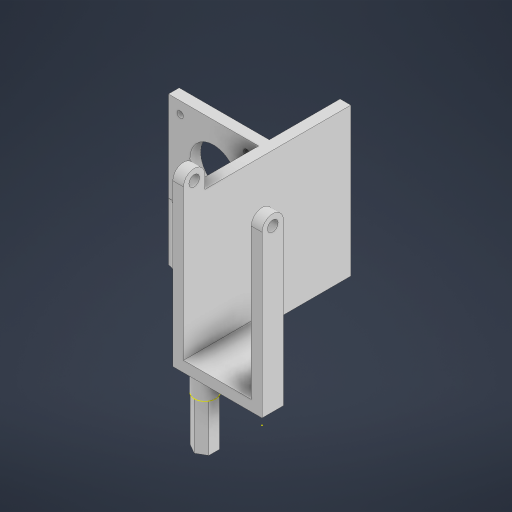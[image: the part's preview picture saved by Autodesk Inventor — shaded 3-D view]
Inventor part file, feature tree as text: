
AUTODESK INVENTOR PART (.ipt)
format: ipt  version: 2024.2 (Build 282272000, 272)  size: 648,192 bytes
history: native  units: mm
features: extrude x13, sketch x12, projected_geometry x4, other x3, chamfer x2, fillet x1
ambient origin geometry x8: Origin, YZ Plane, XZ Plane, XY Plane, X Axis, Y Axis, Z Axis, Center Point
bodies: Body1 (feature_tree)
feature tree (35):
  other  "솔리드1"
  extrude  "돌출1"  Depth=5.0mm
  extrude  "돌출2"  Depth=10.0mm
  extrude  "돌출3"  Depth=53.0mm
  extrude  "돌출4"  Depth=10.0mm
  extrude  "돌출5"  Depth=5.0mm TaperAngle=0.0deg
  chamfer  "모따기1"  Distance=10.0mm
  extrude  "돌출6"  Depth=5.0mm
  extrude  "돌출7"  Depth=31.6mm TaperAngle=0.0deg
  extrude  "돌출8"  Depth=10.0mm
  other  "직접 편집1"
  fillet  "모깎기1"  Radius=53.0mm
  extrude  "돌출9"  Depth=5.0mm
  chamfer  "모따기2"  Distance=5.0mm
  sketch  "스케치11"
  extrude  "돌출10"  Depth=30.0mm TaperAngle=0.0deg
  extrude  "돌출11"  Depth=42.0mm
  extrude  "돌출12"  Depth=42.0mm
  extrude  "돌출13"  Depth=3.0mm
  sketch  "스케치1"
  sketch  "스케치2"
  sketch  "스케치3"
  sketch  "스케치4"
  sketch  "스케치5"
  sketch  "스케치6"
  sketch  "스케치7"
  sketch  "스케치8"
  sketch  "스케치9"
  projected_geometry  "투영된 루프1"
  projected_geometry  "투영된 루프2"
  sketch  "스케치12"
  projected_geometry  "투영된 루프3"
  sketch  "스케치13"
  projected_geometry  "투영된 루프4"
  other  "이동1"
